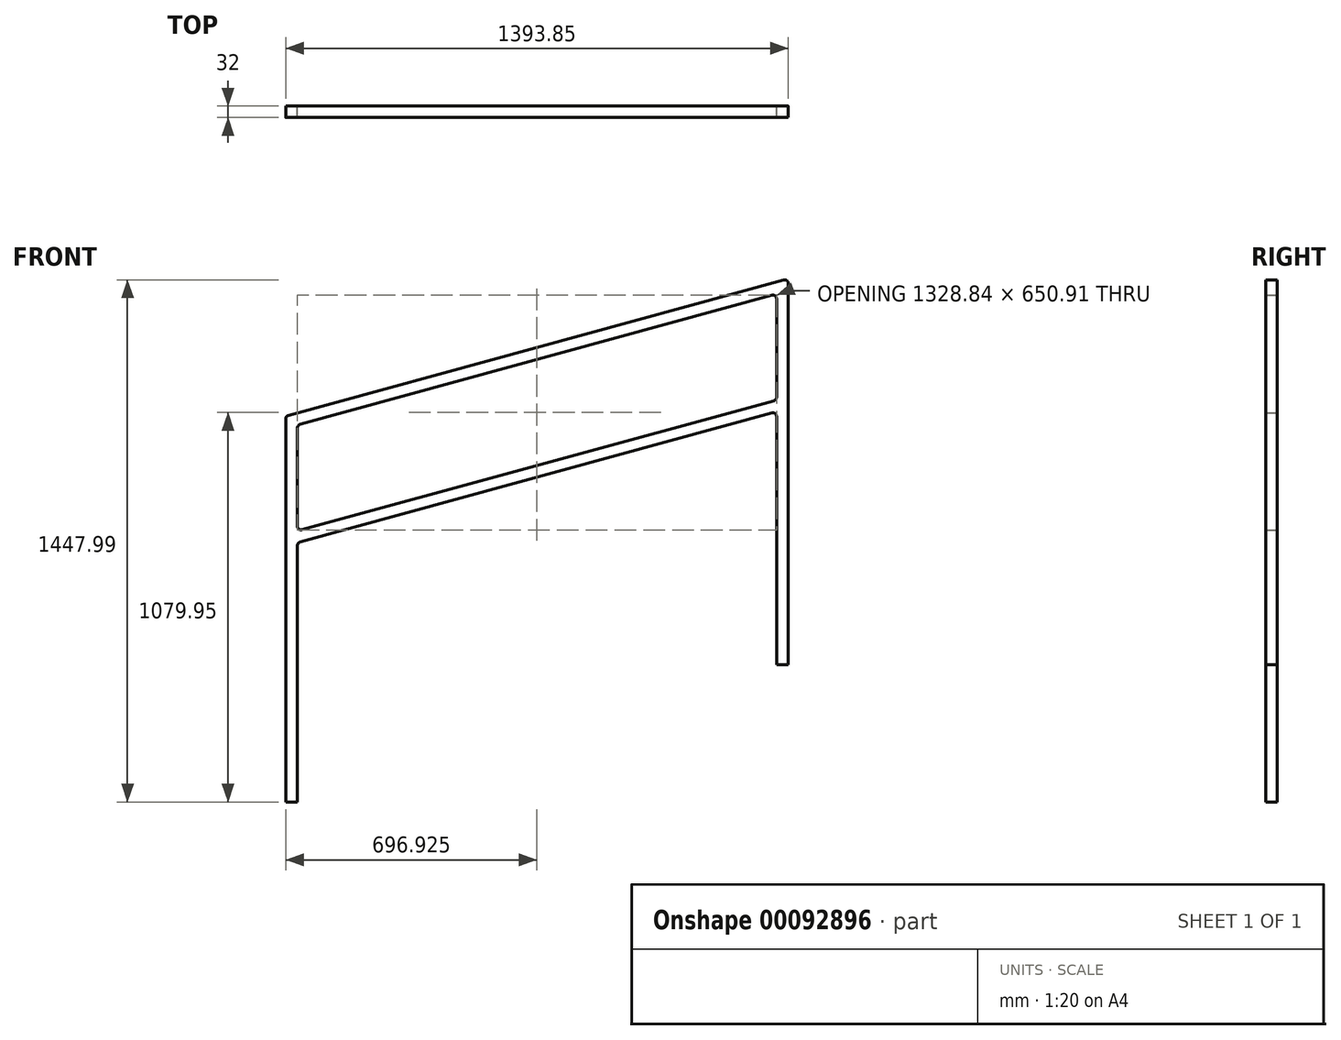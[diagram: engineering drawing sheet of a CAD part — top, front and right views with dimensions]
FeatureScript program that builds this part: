
annotation { "Feature Type Name" : "Feature", "Feature Type Description" : "" }
export const myFeature = defineFeature(function(context is Context, id is Id, definition is map)
    precondition{}
    {
        {
            var Q0;
            Q0=qCreatedBy(makeId("Front.planeOp"),FACE);
            var sketch = newSketch(context, id + "F0", { "sketchPlane" : qUnion([Q0])});
            skLineSegment(sketch, "E0", {"start": v(-255.05, -742.5) * mm, "end": v(-255.05, 319.87) * mm});
            skLineSegment(sketch, "E1", {"start": v(-215.18, -21.6) * mm, "end": v(1093.66, 336.25) * mm});
            skLineSegment(sketch, "E2", {"start": v(-247.68, 329.51) * mm, "end": v(1126.16, 705.13) * mm});
            skLineSegment(sketch, "E3", {"start": v(1138.8, 695.49) * mm, "end": v(1138.8, -361.41) * mm});
            skLineSegment(sketch, "E4.0", {"start": v(1106.3, 652.9) * mm, "end": v(1106.3, 379.83) * mm});
            skLineSegment(sketch, "E4.1", {"start": v(-215.18, 304.7) * mm, "end": v(1093.66, 662.55) * mm});
            skLineSegment(sketch, "E4.2", {"start": v(-222.55, -742.5) * mm, "end": v(-222.55, -31.25) * mm});
            skLineSegment(sketch, "E5", {"start": v(-209.9, 12.34) * mm, "end": v(1098.93, 370.19) * mm});
            skLineSegment(sketch, "E6", {"start": v(-255.05, -742.5) * mm, "end": v(-222.55, -742.5) * mm});
            skLineSegment(sketch, "E7", {"start": v(1106.3, -361.41) * mm, "end": v(1138.8, -361.41) * mm});
            skPoint(sketch, "E8.visualSharp", {"position": v(1138.8, 708.59) * mm});
            skArc(sketch, "E8.filletArc", {"start": v(1138.8, 695.49) * mm, "mid": v(1134.86, 703.44) * mm, "end": v(1126.16, 705.13) * mm});
            skPoint(sketch, "E9.visualSharp", {"position": v(-255.05, 327.5) * mm});
            skArc(sketch, "E9.filletArc", {"start": v(-247.68, 329.51) * mm, "mid": v(-253, 325.93) * mm, "end": v(-255.05, 319.87) * mm});
            skPoint(sketch, "E10.orphan", {"position": v(1138.8, 348.59) * mm});
            skLineSegment(sketch, "E11.trimOffspring", {"start": v(1106.3, 326.6) * mm, "end": v(1106.3, -361.41) * mm});
            skLineSegment(sketch, "E12.trimOffspring", {"start": v(-222.55, 21.99) * mm, "end": v(-222.55, 295.06) * mm});
            skPoint(sketch, "E13.orphan", {"position": v(-255.05, -32.5) * mm});
            skPoint(sketch, "E14.orphan", {"position": v(-255.05, 0) * mm});
            skPoint(sketch, "E15.visualSharp", {"position": v(-222.55, 8.89) * mm});
            skArc(sketch, "E15.filletArc", {"start": v(-222.55, 21.99) * mm, "mid": v(-218.61, 14.04) * mm, "end": v(-209.9, 12.34) * mm});
            skPoint(sketch, "E16.visualSharp", {"position": v(-222.55, -23.61) * mm});
            skArc(sketch, "E16.filletArc", {"start": v(-215.18, -21.6) * mm, "mid": v(-220.5, -25.18) * mm, "end": v(-222.55, -31.25) * mm});
            skPoint(sketch, "E17.visualSharp", {"position": v(-222.55, 302.7) * mm});
            skArc(sketch, "E17.filletArc", {"start": v(-215.18, 304.7) * mm, "mid": v(-220.5, 301.13) * mm, "end": v(-222.55, 295.06) * mm});
            skPoint(sketch, "E18.visualSharp", {"position": v(1106.3, 666) * mm});
            skArc(sketch, "E18.filletArc", {"start": v(1106.3, 652.9) * mm, "mid": v(1102.36, 660.86) * mm, "end": v(1093.66, 662.55) * mm});
            skPoint(sketch, "E19.visualSharp", {"position": v(1106.3, 372.2) * mm});
            skArc(sketch, "E19.filletArc", {"start": v(1098.93, 370.19) * mm, "mid": v(1104.25, 373.77) * mm, "end": v(1106.3, 379.83) * mm});
            skPoint(sketch, "E20.visualSharp", {"position": v(1106.3, 339.7) * mm});
            skArc(sketch, "E20.filletArc", {"start": v(1106.3, 326.6) * mm, "mid": v(1102.36, 334.55) * mm, "end": v(1093.66, 336.25) * mm});
            skSolve(sketch);
        }
        {
            var Q0;
            Q0=makeQuery(id+"F0.imprint","IMPRINT",FACE,{"disambiguationData":[TD([[makeQuery(id+"F0.imprint","IMPRINT",EDGE,{"derivedFrom":sQuery(id+"F0.wireOp",EDGE,"E0")}),-1.0]])]});
            extrude(context, id + "F1", {"entities" : qUnion([Q0]), "endBound" : BoundingType.SYMMETRIC, "depth" : 32 * mm});
        }
    });
